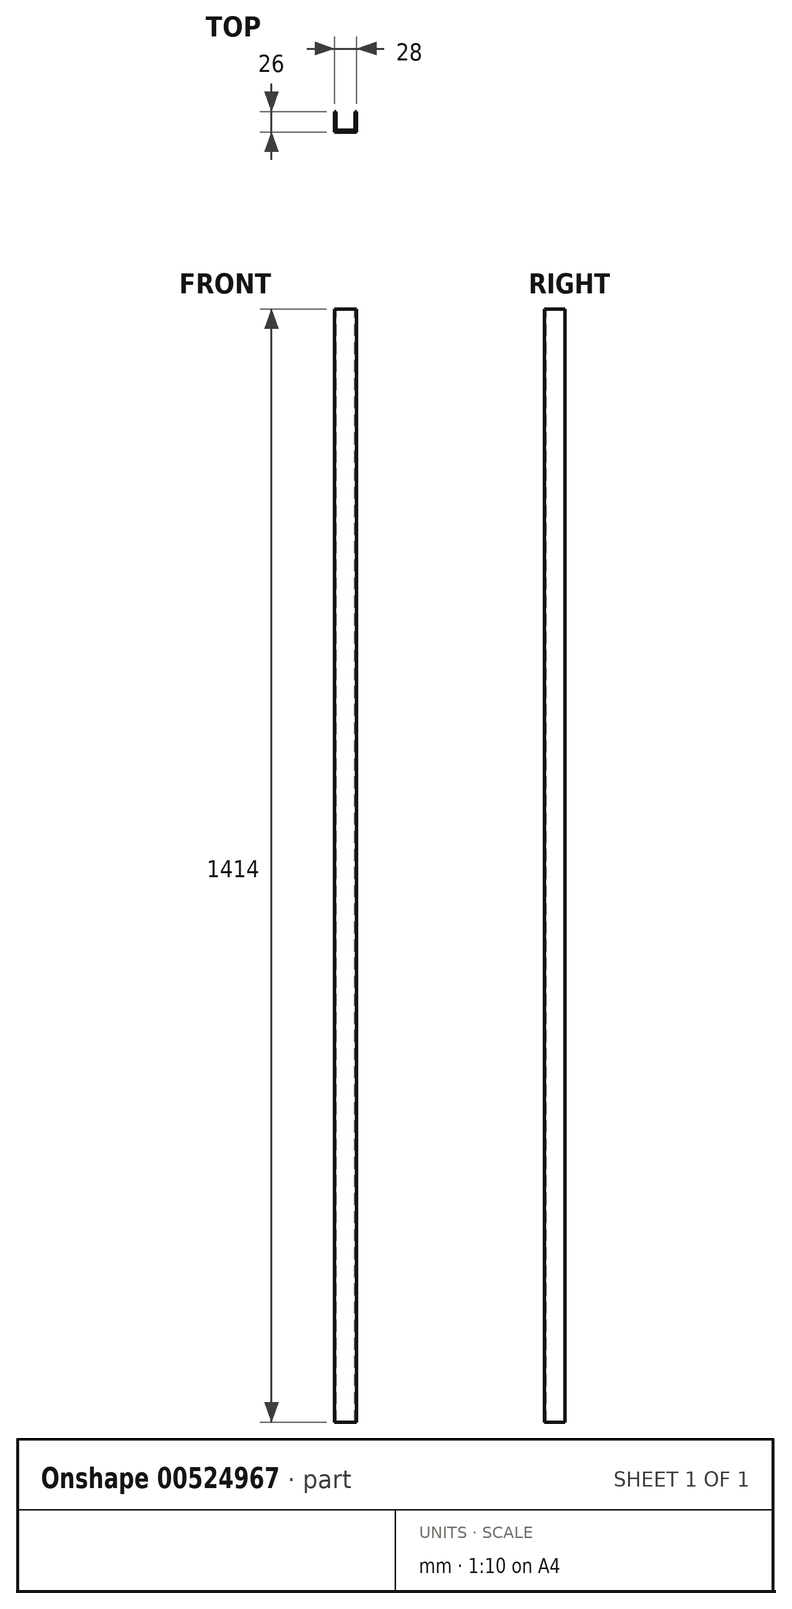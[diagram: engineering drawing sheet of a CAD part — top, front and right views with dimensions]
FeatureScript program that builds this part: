
annotation { "Feature Type Name" : "Feature", "Feature Type Description" : "" }
export const myFeature = defineFeature(function(context is Context, id is Id, definition is map)
    precondition{}
    {
        {
            var Q0;
            Q0=qCreatedBy(makeId("Top.planeOp"),FACE);
            var sketch = newSketch(context, id + "F0", { "sketchPlane" : qUnion([Q0])});
            skLineSegment(sketch, "E0.bottom", {"start": v(0, 0) * mm, "end": v(-28, 0) * mm});
            skLineSegment(sketch, "E0.top", {"start": v(0, 26) * mm, "end": v(-2, 26) * mm});
            skLineSegment(sketch, "E0.left", {"start": v(0, 0) * mm, "end": v(0, 26) * mm});
            skLineSegment(sketch, "E0.right", {"start": v(-28, 0) * mm, "end": v(-28, 26) * mm});
            skLineSegment(sketch, "E1.0", {"start": v(-26, 2) * mm, "end": v(-26, 26) * mm});
            skLineSegment(sketch, "E1.1", {"start": v(-2, 2) * mm, "end": v(-26, 2) * mm});
            skLineSegment(sketch, "E1.2", {"start": v(-2, 2) * mm, "end": v(-2, 26) * mm});
            skLineSegment(sketch, "E2.trimOffspring", {"start": v(-26, 26) * mm, "end": v(-28, 26) * mm});
            skSolve(sketch);
        }
        {
            var Q0;
            Q0 = qSketchRegion(id + "F0", true);
            extrude(context, id + "F1", {"entities" : qUnion([Q0]), "oppositeDirection" : true, "depth" : 1414 * mm, "offsetDistance" : 25 * mm});
        }
    });
